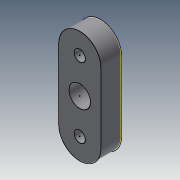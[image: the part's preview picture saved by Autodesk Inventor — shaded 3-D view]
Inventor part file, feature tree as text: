
AUTODESK INVENTOR PART (.ipt)
format: ipt  version: 2015 (Build 190159000, 159)  size: 107,008 bytes
history: native  units: mm
features: other x7, sketch x2, extrude x1, projected_geometry x1
ambient origin geometry x8: Origin, YZ Plane, XZ Plane, XY Plane, X Axis, Y Axis, Z Axis, Center Point
bodies: Body1 (feature_tree)
feature tree (11):
  other  "Blocks"
  extrude  "Extrusion6"  Depth=10.0mm
  sketch  "Sketch10"  dims[d35=10.0mm d36=5.0mm d37=5.0mm d38=10.0mm d39=0.0mm]
  other  "DXF"
  other  "Block1"
  other  "Block2"
  sketch  "Sketch9"  dims[d33=10.0mm d34=33.941125mm]
  projected_geometry  "Projected Loop4"
  other  "Block3"
  other  "Block3:1"
  other  "Block3:2"
